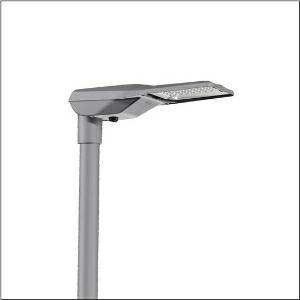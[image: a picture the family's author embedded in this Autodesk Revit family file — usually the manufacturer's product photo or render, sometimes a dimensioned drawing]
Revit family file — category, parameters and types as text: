
# Revit family: streetlight_sl_21_iq_mini___st1_0a_5xe2d31u08gb_76f1
name_source: partatom
category: Lighting Fixtures
units: mm (PartAtom-declared; Revit-internal decimal feet)

## family parameters
Cut with Voids When Loaded = No
Host = Face
Light Source = No
Part Type = Normal
Room Calculation Point = No
Round Connector Dimension = Use Diameter
Shared = No

## types (1)
- --- (1 x LED, 5990 lm, 39.8 W, 3000K)
    Apparent Load = 40 VA
    CIE Flux Codes = 37 72 97 100 100
    Color Rendering = 70
    Color Temperature = 3000K
    Default Elevation = 1800 mm
    Description = Streetlight SL 21 iQ mini, mast luminaire, primary light control with lens, of PMMA, primary optical cover: cover, of toughened safety glass, transparent, light distribution: ST1.0a, light emission: direct distribution, primary light characteristic: asymmetric, installation type: post-top, side-entry, LED, High Power LED, rated luminous flux: 5.990lm, luminous efficacy: 151lm/W, light colour: 730, colour temperature: 3000K, control gear: iQ-Street Remote, D4i with power reduction, control: pre-setting: logarithmic dimming characteristic, Street-Remote, Auto-Match, Temp-Guard, Lumen-Switch, Night-Set, Smart-Wire, Light-Fading, Desk-Remote (wireless, voltage-free reading and setting of iQ features in the workshop via application-optimized NFC function/RFID function), optimised constant luminous flux control (CLO 2.0), mains connection: 220..240V, AC, 50/60Hz, start of lifetime: 40W, end of service life: 41W, reduction: 18W, luminaire housing, of diecast aluminium, powder-coated, Siteco® metallic grey (DB 702S), corrosivity category C5 mid according to DIN EN ISO 12944, please order mast flange separately, inclination adjustable: 0°, 5°, 10°, 15°, sealing non-destructively replaceable, multi-level sealing system, length: 628mm, width: 235mm, height: 110mm, mast flange for spigot size: 42mm (side-entry): 5XC10008XM4, 60/48mm (side-entry/post-top): 5XC10108XM2, 76/60mm (side-entry/post-top): 5XC10108XM1, mounting height: 4..8m, Smart Interface below, protection rating (complete): IP66, insulation class (complete): insulation class II (safety insulation), certification: CE, ENEC, ENEC+, VDE, impact resistance: IK10, permissible operating ambient temperature for outdoor applications: -40..+50°C, standard-compliant lighting for roads and squares, packaging unit: 1 piece

Light Distribution: ST1.0a
    Height = 110 mm
    Lamp = 1 x LED
    Lamp Light Flux = 5990 lm
    Lamp Power = 39.8 W
    Lamp count = 1
    Length = 625 mm
    Luminous efficacy = 151 lm/W
    Manufacturer = Siteco
    ModVariant = No
    Model = 5XE2D31U08GB
    Number of Poles = 1
    OnlyDefault = Yes
    Power Factor = 1
    Product Name = Streetlight SL 21 iQ mini | ST1.0a
    Product group = mast luminaire | pylon top
    ProductGroupID = 6100
    Protection Class = Protection class II
    Protection Degree = IP 66
    RLX_Detail_Level = 1
    RLX_Emergency_Light_Flux = 0 lm
    RLX_Emergency_Type = 0
    RLX_Emergency_Type_DB = No
    RlxData = <blob elided: 26725 chars, md5=0e962224>
    Socket = socket
    Standby Power = 0 W
    System Light Flux = 5990 lm
    System Power = 40 W
    Type Comments = factory setting: luminous flux: 100 % | dim-lin: 254 | 800 mA
    Type Image = l_1003516.jpg
    URL = http://relux.com
    VarID = @adj_115226
    Voltage = 0 V
    Weight = 0.00 kg
    Width = 234 mm

## geometry (parser evidence)
native form markers: Blend x4, Sweep x11
no freeform markers — native parametric forms only
